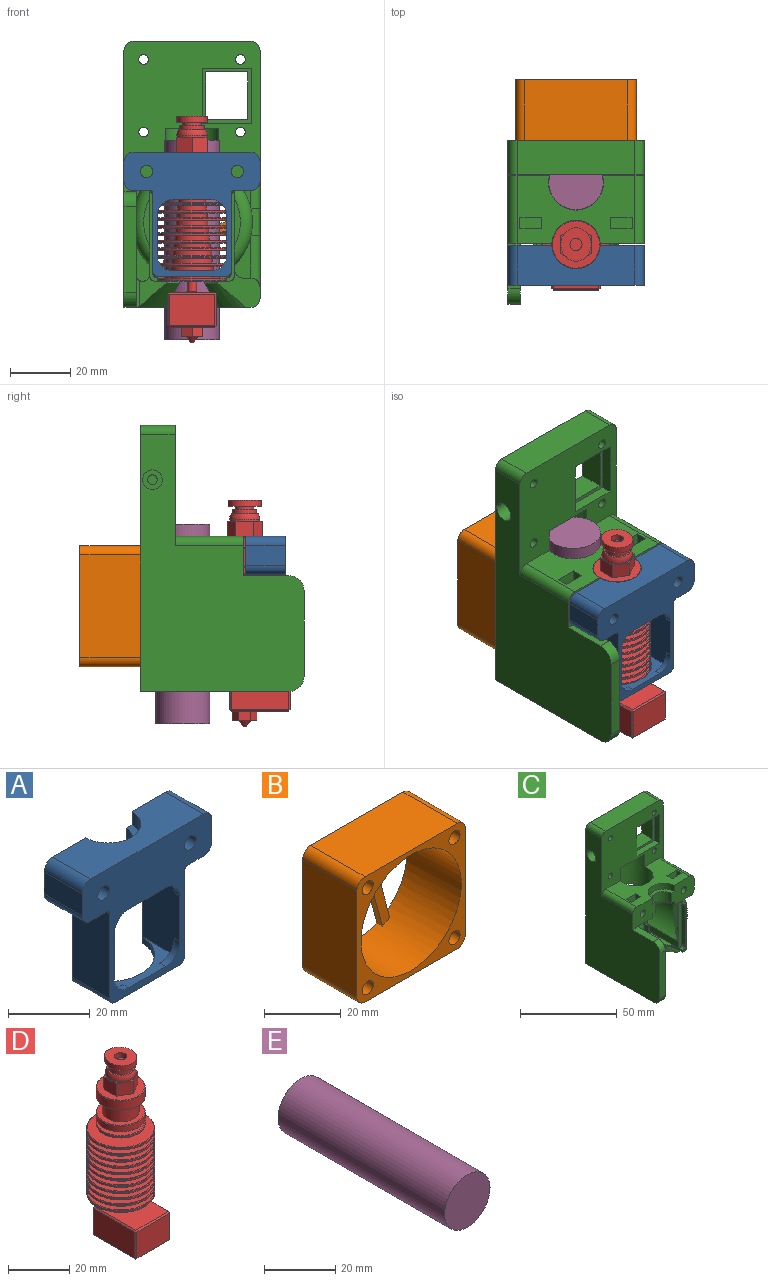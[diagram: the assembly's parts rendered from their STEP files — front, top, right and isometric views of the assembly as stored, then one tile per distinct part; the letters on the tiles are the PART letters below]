
ASSEMBLY  parts=5 mates=8
PART A: 39 faces, bbox 45x13.2x41.2 mm
  f0: plane 5x5mm, normal (0,1,0), area 5.4mm2, adj f15,f24,f26
  f1: plane 26.6x13mm, normal (1,0,0), area 319.8mm2, adj f2,f20,f21,f23,f24,f25,f27,f29
  f2: plane 39x13.2mm, normal (0,0,-1), area 305.9mm2, adj f1,f6,f11,f12,f15,f18,f20,f21
  f3: plane 39x13.2mm, normal (0,0,1), area 419.1mm2, adj f10,f11,f12,f21,f32,f33
  f4: plane 13.2x6.6mm, normal (1,0,0), area 87.1mm2, adj f11,f21,f31,f32
  f5: plane 13.2x6.6mm, normal (-1,0,0), area 87.1mm2, adj f12,f21,f33,f34
  f6: cylinder r=8mm len=15.99mm, axis (0,0,-1), area 63.8mm2, adj f2,f7,f11,f12
  f7: plane 15.99x7.7mm, normal (0,0,-1), area 42.8mm2, adj f6,f8,f11,f12
  f8: cylinder r=6mm len=11.99mm, axis (0,0,-1), area 109.5mm2, adj f7,f9,f11,f12
  f9: plane 15.99x7.7mm, normal (0,0,1), area 42.8mm2, adj f8,f10,f11,f12
  f10: cylinder r=8mm len=15.99mm, axis (0,0,-1), area 98.1mm2, adj f3,f9,f11,f12
  f11: plane 16.51x12.6mm, normal (0,1,0), area 177.7mm2, adj f2,f3,f4,f6,f7,f8,f9,f10
  f12: plane 16.51x12.6mm, normal (0,1,0), area 177.7mm2, adj f2,f3,f5,f6,f7,f8,f9,f10
  f13: cylinder r=2.05mm len=13.2mm, axis (0,-1,0), area 170mm2, adj f12,f21
  f14: cylinder r=2.05mm len=13.2mm, axis (0,-1,0), area 170mm2, adj f11,f21
  f15: plane 26.6x13mm, normal (-1,0,0), area 319.8mm2, adj f0,f2,f18,f21,f23,f24,f26,f28
  f16: plane 22x10.51mm, normal (0,0,-1), area 94.5mm2, adj f21,f30,f35,f36
  f17: plane 25.6x13mm, normal (1,0,0), area 332.8mm2, adj f18,f21,f36,f38
  f18: plane 28.56x2.61mm, normal (0,1,0), area 45.1mm2, adj f2,f15,f17,f24,f30,f36,f38
  f19: plane 25.6x13mm, normal (-1,0,0), area 332.8mm2, adj f20,f21,f35,f37
  f20: plane 28.56x2.61mm, normal (0,1,0), area 45.1mm2, adj f1,f2,f19,f24,f30,f35,f37
  f21: plane 45x41.2mm, normal (0,-1,0), area 758.6mm2, adj f1,f2,f3,f4,f5,f13,f14,f15
  f22: plane 12.8x2mm, normal (0,0,-1), area 25.6mm2, adj f21,f23,f28,f29
  f23: plane 22.8x8mm, normal (0,1,0), area 79.1mm2, adj f1,f2,f15,f22,f28,f29
  f24: plane 22.8x13mm, normal (0,0,1), area 83.7mm2, adj f0,f1,f15,f18,f20,f21,f25,f26
  f25: plane 5x5mm, normal (0,1,0), area 5.4mm2, adj f1,f24,f27
  f26: cylinder r=5mm len=5mm, axis (0,-1,0), area 15.7mm2, adj f0,f15,f21,f24
  f27: cylinder r=5mm len=5mm, axis (0,1,0), area 15.7mm2, adj f1,f21,f24,f25
  f28: cylinder r=5mm len=5mm, axis (0,1,0), area 15.7mm2, adj f15,f21,f22,f23
  f29: cylinder r=5mm len=5mm, axis (0,-1,0), area 15.7mm2, adj f1,f21,f22,f23
  f30: cylinder r=11.4mm len=22.78mm, axis (0,0,-1), area 69.5mm2, adj f16,f18,f20,f24,f35,f36
  f31: cylinder r=3mm len=13.2mm, axis (0,-1,0), area 62.2mm2, adj f2,f4,f11,f21
  f32: cylinder r=3mm len=13.2mm, axis (0,1,0), area 62.2mm2, adj f3,f4,f11,f21
  f33: cylinder r=3mm len=13.2mm, axis (0,-1,0), area 62.2mm2, adj f3,f5,f12,f21
  f34: cylinder r=3mm len=13.2mm, axis (0,1,0), area 62.2mm2, adj f2,f5,f12,f21
  f35: cylinder r=2mm len=13mm, axis (0,1,0), area 40.2mm2, adj f16,f19,f20,f21,f30
  f36: cylinder r=2mm len=13mm, axis (0,-1,0), area 40.2mm2, adj f16,f17,f18,f21,f30
  f37: cylinder r=1mm len=13mm, axis (0,-1,0), area 20.4mm2, adj f2,f19,f20,f21
  f38: cylinder r=1mm len=13mm, axis (0,1,0), area 20.4mm2, adj f2,f17,f18,f21
PART B: 25 faces, bbox 40x20x40 mm
  f0: plane 34x20mm, normal (0,0,-1), area 680mm2, adj f9,f10,f21,f24
  f1: plane 34x20mm, normal (1,0,0), area 680mm2, adj f9,f10,f21,f22
  f2: plane 34x20mm, normal (0,0,1), area 680mm2, adj f9,f10,f22,f23
  f3: cylinder r=18.5mm len=37mm, axis (0,1,0), area 2306.3mm2, adj f9,f10,f12,f13,f15,f16,f18,f19
  f4: cylinder r=2.05mm len=20mm, axis (0,1,0), area 257.6mm2, adj f9,f10
  f5: cylinder r=2.05mm len=20mm, axis (0,1,0), area 257.6mm2, adj f9,f10
  f6: cylinder r=2.05mm len=20mm, axis (0,1,0), area 257.6mm2, adj f9,f10
  f7: cylinder r=2.05mm len=20mm, axis (0,1,0), area 257.6mm2, adj f9,f10
  f8: plane 34x20mm, normal (-1,0,0), area 680mm2, adj f9,f10,f23,f24
  f9: plane 40x40mm, normal (0,-1,0), area 464.3mm2, adj f0,f1,f2,f3,f4,f5,f6,f7
  f10: plane 40x40mm, normal (0,1,0), area 702.9mm2, adj f0,f1,f2,f3,f4,f5,f6,f7
  f11: cylinder r=6mm len=5.91mm, axis (0,1,0), area 15.5mm2, adj f10,f12,f19,f20
  f12: plane 9.16x9.16mm, normal (0.71,0,-0.71), area 25.9mm2, adj f3,f10,f11,f20
  f13: plane 11.21x11.21mm, normal (-0.71,0,0.71), area 31.7mm2, adj f3,f10,f14,f20
  f14: cylinder r=6mm len=6.56mm, axis (0,1,0), area 15.5mm2, adj f10,f13,f15,f20
  f15: plane 12.52x3.35mm, normal (0.26,0,0.97), area 25.9mm2, adj f3,f10,f14,f20
  f16: plane 15.31x4.1mm, normal (-0.26,0,-0.97), area 31.7mm2, adj f3,f10,f17,f20
  f17: cylinder r=6mm len=7.2mm, axis (0,1,0), area 15.5mm2, adj f10,f16,f18,f20
  f18: plane 12.52x3.35mm, normal (-0.97,0,-0.26), area 25.9mm2, adj f3,f10,f17,f20
  f19: plane 15.31x4.1mm, normal (0.97,0,0.26), area 31.7mm2, adj f3,f10,f11,f20
  f20: plane 33.46x29.5mm, normal (0,-1,0), area 238.6mm2, adj f3,f11,f12,f13,f14,f15,f16,f17
  f21: cylinder r=3mm len=20mm, axis (0,-1,0), area 94.2mm2, adj f0,f1,f9,f10
  f22: cylinder r=3mm len=20mm, axis (0,1,0), area 94.2mm2, adj f1,f2,f9,f10
  f23: cylinder r=3mm len=20mm, axis (0,-1,0), area 94.2mm2, adj f2,f8,f9,f10
  f24: cylinder r=3mm len=20mm, axis (0,1,0), area 94.2mm2, adj f0,f8,f9,f10
PART C: 147 faces, bbox 46.5x58.5x89.5 mm
  f0: plane 11.9x4.4mm, normal (0,-1,0), area 34.1mm2, adj f2,f5,f19,f109,f141,f145
  f1: plane 10.46x9.18mm, normal (0,-1,0), area 42.6mm2, adj f5,f65,f88,f102,f107,f109,f144,f145
  f2: cylinder r=20mm len=22.2mm, axis (0,1,0), area 177mm2, adj f0,f4,f19,f141
  f3: cylinder r=20mm len=22.2mm, axis (0,1,0), area 72.4mm2, adj f4,f21,f22,f141
  f4: torus R=16mm, axis (0,-1,0), area 107.7mm2, adj f2,f3,f19,f21,f23,f28,f84,f106
  f5: plane 18.7x0.4mm, normal (0,0,1), area 7.5mm2, adj f0,f1,f109,f145
  f6: plane 88.6x45.6mm, normal (0,1,0), area 2644.8mm2, adj f11,f12,f13,f14,f16,f26,f46,f47
  f7: plane 28.3x4mm, normal (0,-1,0), area 113.2mm2, adj f46,f141,f142,f143
  f8: cylinder r=1.6mm len=7.6mm, axis (1,0,0), area 76.4mm2, adj f134,f137
  f9: cylinder r=1.6mm len=7mm, axis (1,0,0), area 70.4mm2, adj f13,f136
  f10: plane 45x39.7mm, normal (0,-1,0), area 1182.7mm2, adj f15,f16,f38,f46,f47,f98,f99,f123
  f11: plane 15.8x8mm, normal (-1,0,0), area 126.4mm2, adj f6,f12,f14,f133
  f12: plane 13.9x8mm, normal (0,0,1), area 111.2mm2, adj f6,f11,f13,f133
  f13: plane 15.8x8mm, normal (1,0,0), area 118.4mm2, adj f6,f9,f12,f14,f133
  f14: plane 13.9x8mm, normal (0,0,-1), area 111.2mm2, adj f6,f11,f13,f133
  f15: plane 39x22.7mm, normal (0,0,1), area 560.6mm2, adj f10,f27,f28,f38,f40,f50,f51,f52
  f16: plane 82x34.2mm, normal (1,0,0), area 864.4mm2, adj f6,f10,f27,f92,f93,f94,f95,f96
  f17: cylinder r=1.6mm len=4.4mm, axis (1,0,0), area 44.2mm2, adj f120,f121
  f18: plane 5x2.15mm, normal (-1,0,0), area 10.7mm2, adj f112,f113,f114,f118
  f19: plane 29.2x27.6mm, normal (-1,0,0), area 175mm2, adj f0,f2,f4,f23,f85,f102,f106,f109
  f20: plane 26.2x0.4mm, normal (1,0,0), area 10.5mm2, adj f21,f22,f28,f90
  f21: plane 26.2x8.43mm, normal (0,0,-1), area 95.2mm2, adj f3,f4,f20,f22,f28
  f22: plane 3.48x2.9mm, normal (0,-1,0), area 2.8mm2, adj f3,f20,f21,f90,f141
  f23: plane 15.13x1.9mm, normal (0,-1,0), area 19.4mm2, adj f4,f19
  f24: plane 15.13x1.9mm, normal (0,-1,0), area 19.4mm2, adj f76,f100
  f25: plane 6.06x2.48mm, normal (0,-1,0), area 6.3mm2, adj f32,f75,f93
  f26: plane 49.15x42mm, normal (0,0,-1), area 738mm2, adj f6,f46,f63,f68,f97,f107,f108,f115
  f27: plane 41.59x16.51mm, normal (0,-1,0), area 228.3mm2, adj f15,f16,f31,f32,f39,f40,f41,f42
  f28: plane 41.59x16.51mm, normal (0,-1,0), area 231mm2, adj f4,f15,f20,f21,f31,f40,f41,f42
  f29: plane 3.8x0.1mm, normal (0,1,0), area 0.2mm2, adj f69,f80
  f30: plane 18.7x2.4mm, normal (0,0,1), area 44.9mm2, adj f36,f68,f91,f96
  f31: plane 26.2x23.77mm, normal (0,0,-1), area 294.8mm2, adj f27,f28,f38,f44,f70,f73,f74,f77
  f32: plane 26.2x7.43mm, normal (0,0,-1), area 69mm2, adj f25,f27,f75,f92,f100
  f33: plane 24.37x7.02mm, normal (0,0,1), area 75mm2, adj f34,f63,f64,f65,f104
  f34: plane 4.56x3.93mm, normal (0,-1,0), area 11.3mm2, adj f33,f63,f69,f78,f104
  f35: plane 4.56x3.93mm, normal (0,-1,0), area 11.3mm2, adj f37,f63,f69,f73,f103
  f36: plane 14.06x5.4mm, normal (0,-1,0), area 41.8mm2, adj f30,f75,f76,f91,f95
  f37: plane 24.37x7.02mm, normal (0,0,1), area 75mm2, adj f35,f63,f66,f67,f103
  f38: cylinder r=9.1mm len=20.6mm, axis (0,0,1), area 886.5mm2, adj f10,f15,f31,f70,f146
  f39: cylinder r=2.05mm len=5mm, axis (0,-1,0), area 64.4mm2, adj f27,f54
  f40: cylinder r=8mm len=15.99mm, axis (0,0,-1), area 98.1mm2, adj f15,f27,f28,f41
  f41: plane 15.99x7.7mm, normal (0,0,1), area 42.8mm2, adj f27,f28,f40,f42
  f42: cylinder r=6mm len=11.99mm, axis (0,0,-1), area 109.5mm2, adj f27,f28,f41,f43
  f43: plane 15.99x7.7mm, normal (0,0,-1), area 42.8mm2, adj f27,f28,f42,f44
  f44: cylinder r=8mm len=15.99mm, axis (0,0,-1), area 63.8mm2, adj f27,f28,f31,f43
  f45: plane 10.34x3.7mm, normal (1,0,0), area 36.7mm2, adj f68,f96,f97,f122
  f46: plane 85x54.15mm, normal (-1,0,0), area 2794.1mm2, adj f6,f7,f10,f26,f28,f90,f99,f123
  f47: plane 39x11.5mm, normal (0,0,1), area 448.5mm2, adj f6,f10,f98,f99
  f48: cylinder r=2.05mm len=5mm, axis (0,-1,0), area 64.4mm2, adj f28,f51
  f49: plane 7.1x3.8mm, normal (0,0,1), area 27mm2, adj f50,f51,f52,f53
  f50: plane 10.8x3.8mm, normal (-1,0,0), area 41mm2, adj f15,f49,f51,f53
  f51: plane 10.8x7.1mm, normal (0,1,0), area 63.5mm2, adj f15,f48,f49,f50,f52
  f52: plane 10.8x3.8mm, normal (1,0,0), area 41mm2, adj f15,f49,f51,f53
  f53: plane 10.8x7.1mm, normal (0,-1,0), area 63.5mm2, adj f15,f49,f50,f52,f60
  f54: plane 10.8x7.1mm, normal (0,1,0), area 63.5mm2, adj f15,f39,f56,f57,f58
  f55: plane 10.8x7.1mm, normal (0,-1,0), area 63.5mm2, adj f15,f56,f57,f58,f62
  f56: plane 7.1x3.8mm, normal (0,0,1), area 27mm2, adj f54,f55,f57,f58
  f57: plane 10.8x3.8mm, normal (1,0,0), area 41mm2, adj f15,f54,f55,f56
  f58: plane 10.8x3.8mm, normal (-1,0,0), area 41mm2, adj f15,f54,f55,f56
  f59: plane 4.1x4.1mm, normal (0,-1,0), area 13.2mm2, adj f60
  f60: cylinder r=2.05mm len=4.1mm, axis (0,-1,0), area 30.9mm2, adj f53,f59
  f61: plane 4.1x4.1mm, normal (0,-1,0), area 13.2mm2, adj f62
  f62: cylinder r=2.05mm len=4.1mm, axis (0,-1,0), area 30.9mm2, adj f55,f61
  f63: cylinder r=9.1mm len=18.2mm, axis (0,0,1), area 333.8mm2, adj f26,f33,f34,f35,f37,f64,f66,f69
  f64: plane 7.52x4.9mm, normal (0.82,0.57,0), area 25.6mm2, adj f33,f63,f65,f107
  f65: cylinder r=11.4mm len=10.61mm, axis (0,0,-1), area 17.2mm2, adj f1,f33,f64,f88,f89,f104,f107
  f66: plane 7.52x4.9mm, normal (-0.82,0.57,0), area 25.6mm2, adj f37,f63,f67,f108
  f67: cylinder r=11.4mm len=10.61mm, axis (0,0,-1), area 17.2mm2, adj f37,f66,f68,f86,f87,f103,f108
  f68: plane 15.69x14.21mm, normal (0,-1,0), area 91.6mm2, adj f26,f30,f45,f67,f76,f86,f91,f96
  f69: cylinder r=18.5mm len=37mm, axis (0,-1,0), area 1412.8mm2, adj f6,f29,f34,f35,f63,f71,f72,f73
  f70: plane 23.77x8mm, normal (0,0.57,-0.82), area 151.8mm2, adj f6,f31,f38,f71,f72
  f71: bspline ~13.74x11.32mm, area 62.1mm2, adj f6,f69,f70,f74
  f72: bspline ~13.74x11.32mm, area 62.1mm2, adj f6,f69,f70,f77
  f73: plane 28.99x26.2mm, normal (-1,0,0), area 132.8mm2, adj f27,f31,f35,f69,f81,f103
  f74: extruded ~24.31x5.61mm, area 150.1mm2, adj f31,f69,f71,f81
  f75: cylinder r=20mm len=24.68mm, axis (0,1,0), area 595.4mm2, adj f25,f32,f36,f76,f94,f100
  f76: plane 29.2x27.6mm, normal (1,0,0), area 137.6mm2, adj f24,f36,f68,f75,f83,f91,f100,f101
  f77: extruded ~24.31x5.61mm, area 155.1mm2, adj f31,f69,f72,f80
  f78: plane 28.99x26.2mm, normal (1,0,0), area 132.8mm2, adj f28,f31,f34,f69,f80,f104
  f79: plane 3.8x0.1mm, normal (0,1,0), area 0.2mm2, adj f69,f81
  f80: plane 26.43x11.36mm, normal (0.82,0.57,0), area 231.6mm2, adj f29,f31,f69,f77,f78
  f81: plane 25.41x10.34mm, normal (-0.82,0.57,0), area 231.6mm2, adj f31,f69,f73,f74,f79
  f82: plane 25.61x3mm, normal (-1,0,0), area 76.8mm2, adj f27,f83,f100,f103,f105
  f83: plane 29.6x2.7mm, normal (0,-1,0), area 28.2mm2, adj f76,f82,f86,f87,f101,f103,f105
  f84: plane 25.61x3mm, normal (1,0,0), area 76.8mm2, adj f4,f28,f85,f104,f106
  f85: plane 29.6x2.7mm, normal (0,-1,0), area 28.2mm2, adj f19,f84,f88,f89,f102,f104,f106
  f86: plane 10.5x3.78mm, normal (0,0,-1), area 14.9mm2, adj f67,f68,f83,f87,f101
  f87: plane 2.7x1.01mm, normal (-1,0,0), area 2.7mm2, adj f67,f83,f86,f103
  f88: plane 10.5x3.78mm, normal (0,0,-1), area 14.9mm2, adj f1,f65,f85,f89,f102
  f89: plane 2.7x1.01mm, normal (1,0,0), area 2.7mm2, adj f65,f85,f88,f104
  f90: plane 41.15x4mm, normal (0,0,1), area 112.2mm2, adj f20,f22,f28,f46,f141,f143
  f91: cylinder r=3mm len=18.7mm, axis (0,1,0), area 88.1mm2, adj f30,f36,f68,f76
  f92: cylinder r=3mm len=29.2mm, axis (0,1,0), area 130.5mm2, adj f16,f27,f32,f93
  f93: cylinder r=3mm len=9.06mm, axis (0,0,-1), area 35.6mm2, adj f16,f25,f92,f94
  f94: bspline ~11.65x3.39mm, area 38.9mm2, adj f16,f75,f93,f95
  f95: cylinder r=3mm len=17.06mm, axis (0,0,-1), area 73.3mm2, adj f16,f36,f94,f96
  f96: cylinder r=3mm len=21.7mm, axis (0,-1,0), area 92.4mm2, adj f16,f30,f45,f68,f95,f122
  f97: cylinder r=3mm len=26.7mm, axis (0,-1,0), area 122mm2, adj f6,f16,f26,f45,f68,f122
  f98: cylinder r=3mm len=11.5mm, axis (0,1,0), area 54.2mm2, adj f6,f10,f16,f47
  f99: cylinder r=3mm len=11.5mm, axis (0,-1,0), area 54.2mm2, adj f6,f10,f46,f47
  f100: torus R=16mm, axis (0,-1,0), area 150.7mm2, adj f24,f27,f32,f75,f76,f82,f105
  f101: cylinder r=2mm len=10.5mm, axis (0,1,0), area 33mm2, adj f68,f76,f83,f86
  f102: cylinder r=2mm len=10.5mm, axis (0,1,0), area 33mm2, adj f1,f19,f85,f88
  f103: cylinder r=2mm len=29.2mm, axis (0,1,0), area 13.9mm2, adj f27,f35,f37,f67,f73,f82,f83,f87
  f104: cylinder r=2mm len=29.2mm, axis (0,-1,0), area 13.9mm2, adj f28,f33,f34,f65,f78,f84,f85,f89
  f105: cylinder r=1mm len=3.23mm, axis (0,-1,0), area 4.6mm2, adj f76,f82,f83,f100
  f106: cylinder r=1mm len=3.23mm, axis (0,-1,0), area 4.6mm2, adj f4,f19,f84,f85
  f107: cone r=11.4mm half-angle=45deg, axis (0,0,-1), area 105.5mm2, adj f1,f26,f63,f64,f65,f144
  f108: cone r=11.4mm half-angle=45deg, axis (0,0,-1), area 99.4mm2, adj f26,f63,f66,f67,f68
  f109: cylinder r=2mm len=18.7mm, axis (0,-1,0), area 58.8mm2, adj f0,f1,f5,f19
  f110: plane 5x4mm, normal (0,1,0), area 20mm2, adj f63,f111,f113,f114
  f111: plane 5x2.15mm, normal (-1,0,0), area 10.7mm2, adj f110,f113,f114,f119
  f112: plane 5x4mm, normal (0,-1,0), area 20mm2, adj f18,f63,f113,f114
  f113: plane 10x4mm, normal (0,0,-1), area 29.8mm2, adj f18,f63,f110,f111,f112,f117
  f114: plane 10x4mm, normal (0,0,1), area 29.8mm2, adj f18,f63,f110,f111,f112,f115
  f115: plane 5.7x2.35mm, normal (1,0,0), area 13.4mm2, adj f26,f114,f118,f119
  f116: plane 5.7x2.5mm, normal (0,0,-1), area 14.3mm2, adj f117,f118,f119,f120
  f117: plane 5.7x2.35mm, normal (1,0,0), area 13.4mm2, adj f113,f116,f118,f119
  f118: plane 9.7x2.5mm, normal (0,-1,0), area 24.3mm2, adj f18,f26,f115,f116,f117,f120
  f119: plane 9.7x2.5mm, normal (0,1,0), area 24.3mm2, adj f26,f111,f115,f116,f117,f120
  f120: plane 9.7x5.7mm, normal (-1,0,0), area 47.2mm2, adj f17,f26,f116,f118,f119
  f121: plane 6x6mm, normal (1,0,0), area 20.2mm2, adj f17,f122
  f122: cylinder r=3mm len=6mm, axis (1,0,0), area 74.8mm2, adj f16,f45,f96,f97,f121
  f123: cylinder r=3mm len=22.7mm, axis (0,1,0), area 107mm2, adj f10,f15,f28,f46
  f124: cylinder r=3mm len=22.7mm, axis (0,-1,0), area 107mm2, adj f10,f15,f16,f27
  f125: cylinder r=1.6mm len=11.5mm, axis (0,1,0), area 115.6mm2, adj f6,f10
  f126: cylinder r=1.6mm len=11.5mm, axis (0,1,0), area 115.6mm2, adj f6,f10
  f127: cylinder r=1.6mm len=11.5mm, axis (0,1,0), area 115.6mm2, adj f6,f10
  f128: cylinder r=1.6mm len=11.5mm, axis (0,1,0), area 115.6mm2, adj f6,f10
  f129: plane 18.2x3.5mm, normal (-1,0,0), area 63.7mm2, adj f10,f130,f132,f133
  f130: plane 16.3x3.5mm, normal (0,0,1), area 57mm2, adj f10,f129,f131,f133
  f131: plane 18.2x3.5mm, normal (1,0,0), area 63.7mm2, adj f10,f130,f132,f133
  f132: plane 16.3x3.5mm, normal (0,0,-1), area 57mm2, adj f10,f129,f131,f133
  f133: plane 18.2x16.3mm, normal (0,-1,0), area 77mm2, adj f11,f12,f13,f14,f129,f130,f131,f132
  f134: plane 6.5x6.5mm, normal (-1,0,0), area 25.1mm2, adj f8,f135
  f135: cylinder r=3.25mm len=10mm, axis (-1,0,0), area 204.2mm2, adj f46,f134
  f136: plane 7.5x5.6mm, normal (-1,0,0), area 34mm2, adj f6,f9,f138,f139,f140
  f137: plane 7.5x5.6mm, normal (1,0,0), area 34mm2, adj f6,f8,f138,f139,f140
  f138: plane 7.5x2.5mm, normal (0,0,1), area 18.8mm2, adj f6,f136,f137,f140
  f139: plane 7.5x2.5mm, normal (0,0,-1), area 18.8mm2, adj f6,f136,f137,f140
  f140: plane 5.6x2.5mm, normal (0,1,0), area 14mm2, adj f136,f137,f138,f139
  f141: plane 46.15x38.3mm, normal (1,0,0), area 1170.4mm2, adj f0,f2,f3,f4,f7,f22,f26,f90
  f142: cylinder r=5mm len=5mm, axis (-1,0,0), area 31.4mm2, adj f7,f26,f46,f141
  f143: cylinder r=5mm len=5mm, axis (-1,0,0), area 31.4mm2, adj f7,f46,f90,f141
  f144: cylinder r=1mm len=10.7mm, axis (0,0,1), area 15.4mm2, adj f1,f26,f107,f141,f145
  f145: cylinder r=2mm len=19.7mm, axis (0,1,0), area 59.8mm2, adj f0,f1,f5,f141,f144
  f146: plane 17.5x6.6mm, normal (0,0,-1), area 85.2mm2, adj f10,f38
PART D: 145 faces, bbox 22.3x26.2x74.9 mm
  f0: plane 4.33x2.5mm, normal (0,0,1), area 1.3mm2, adj f130,f131,f134
  f1: plane 5x1.44mm, normal (0,0,1), area 1.3mm2, adj f129,f130,f134
  f2: plane 4.33x2.5mm, normal (0,0,1), area 1.3mm2, adj f128,f129,f134
  f3: plane 4.33x2.5mm, normal (0,0,1), area 1.3mm2, adj f127,f128,f134
  f4: plane 5x1.44mm, normal (0,0,1), area 1.3mm2, adj f127,f132,f134
  f5: plane 19x15mm, normal (0,0,-1), area 242.6mm2, adj f103,f108,f111,f114,f116,f117,f118,f119
  f6: plane 15.6x15.6mm, normal (0,0,1), area 104.5mm2, adj f89,f127,f128,f129,f130,f131,f132
  f7: cylinder r=1.5mm len=3.3mm, axis (0,0,-1), area 31.1mm2, adj f8,f115
  f8: plane 21.9x21.9mm, normal (0,0,-1), area 369.6mm2, adj f7,f62
  f9: cylinder r=11.15mm len=22.3mm, axis (0,0,-1), area 42mm2, adj f62,f63
  f10: plane 21.9x21.9mm, normal (0,0,1), area 200mm2, adj f11,f63
  f11: cylinder r=7.5mm len=15mm, axis (0,0,-1), area 70.7mm2, adj f10,f12
  f12: plane 21.9x21.9mm, normal (0,0,-1), area 200mm2, adj f11,f64
  f13: cylinder r=11.15mm len=22.3mm, axis (0,0,-1), area 42mm2, adj f64,f65
  f14: plane 21.9x21.9mm, normal (0,0,1), area 222.7mm2, adj f15,f65
  f15: cylinder r=7mm len=14mm, axis (0,0,-1), area 66mm2, adj f14,f16
  f16: plane 21.9x21.9mm, normal (0,0,-1), area 222.7mm2, adj f15,f66
  f17: cylinder r=11.15mm len=22.3mm, axis (0,0,-1), area 42mm2, adj f66,f67
  f18: plane 21.9x21.9mm, normal (0,0,1), area 233.5mm2, adj f19,f67
  f19: cylinder r=6.75mm len=13.5mm, axis (0,0,-1), area 63.6mm2, adj f18,f20
  f20: plane 21.9x21.9mm, normal (0,0,-1), area 233.5mm2, adj f19,f68
  f21: cylinder r=11.15mm len=22.3mm, axis (0,0,-1), area 42mm2, adj f68,f69
  f22: plane 21.9x21.9mm, normal (0,0,1), area 244mm2, adj f23,f69
  f23: cylinder r=6.5mm len=13mm, axis (0,0,-1), area 61.3mm2, adj f22,f24
  f24: plane 21.9x21.9mm, normal (0,0,-1), area 244mm2, adj f23,f70
  f25: cylinder r=11.15mm len=22.3mm, axis (0,0,-1), area 42mm2, adj f70,f71
  f26: plane 21.9x21.9mm, normal (0,0,1), area 263.6mm2, adj f27,f71
  f27: cylinder r=6mm len=12mm, axis (0,0,-1), area 56.5mm2, adj f26,f28
  f28: plane 21.9x21.9mm, normal (0,0,-1), area 263.6mm2, adj f27,f72
  f29: cylinder r=11.15mm len=22.3mm, axis (0,0,-1), area 42mm2, adj f72,f73
  f30: plane 21.9x21.9mm, normal (0,0,1), area 272.8mm2, adj f31,f73
  f31: cylinder r=5.75mm len=11.5mm, axis (0,0,-1), area 54.2mm2, adj f30,f32
  f32: plane 21.9x21.9mm, normal (0,0,-1), area 272.8mm2, adj f31,f74
  f33: cylinder r=11.15mm len=22.3mm, axis (0,0,-1), area 42mm2, adj f74,f75
  f34: plane 21.9x21.9mm, normal (0,0,1), area 281.7mm2, adj f35,f75
  f35: cylinder r=5.5mm len=11mm, axis (0,0,-1), area 51.8mm2, adj f34,f36
  f36: plane 21.9x21.9mm, normal (0,0,-1), area 281.7mm2, adj f35,f76
  f37: cylinder r=11.15mm len=22.3mm, axis (0,0,-1), area 42mm2, adj f76,f77
  f38: plane 21.9x21.9mm, normal (0,0,1), area 290.1mm2, adj f39,f77
  f39: cylinder r=5.25mm len=10.5mm, axis (0,0,-1), area 49.5mm2, adj f38,f40
  f40: plane 21.9x21.9mm, normal (0,0,-1), area 290.1mm2, adj f39,f78
  f41: cylinder r=11.15mm len=22.3mm, axis (0,0,-1), area 42mm2, adj f78,f79
  f42: plane 21.9x21.9mm, normal (0,0,1), area 298.1mm2, adj f43,f79
  f43: cylinder r=5mm len=10mm, axis (0,0,-1), area 47.1mm2, adj f42,f44
  f44: plane 21.9x21.9mm, normal (0,0,-1), area 298.1mm2, adj f43,f80
  f45: cylinder r=11.15mm len=22.3mm, axis (0,0,-1), area 42mm2, adj f80,f81
  f46: plane 21.9x21.9mm, normal (0,0,1), area 305.8mm2, adj f47,f81
  f47: cylinder r=4.75mm len=9.5mm, axis (0,0,-1), area 44.8mm2, adj f46,f48
  f48: plane 21.9x21.9mm, normal (0,0,-1), area 305.8mm2, adj f47,f82
  f49: cylinder r=11.15mm len=22.3mm, axis (0,0,-1), area 42mm2, adj f82,f83
  f50: plane 21.9x21.9mm, normal (0,0,1), area 313.1mm2, adj f51,f83
  f51: cylinder r=4.5mm len=9mm, axis (0,0,-1), area 42.4mm2, adj f50,f52
  f52: plane 15.6x15.6mm, normal (0,0,-1), area 127.5mm2, adj f51,f84
  f53: cylinder r=8mm len=16mm, axis (0,0,-1), area 30.2mm2, adj f84,f85
  f54: plane 15.6x15.6mm, normal (0,0,1), area 127.5mm2, adj f55,f85
  f55: cylinder r=4.5mm len=9mm, axis (0,0,-1), area 42.4mm2, adj f54,f56
  f56: plane 15.6x15.6mm, normal (0,0,-1), area 127.5mm2, adj f55,f86
  f57: cylinder r=8mm len=16mm, axis (0,0,-1), area 110.6mm2, adj f86,f87
  f58: plane 15.6x15.6mm, normal (0,0,1), area 78mm2, adj f59,f87
  f59: cylinder r=6mm len=12mm, axis (0,0,-1), area 226.2mm2, adj f58,f60
  f60: plane 15.6x15.6mm, normal (0,0,-1), area 78mm2, adj f59,f88
  f61: cylinder r=8mm len=16mm, axis (0,0,-1), area 181mm2, adj f88,f89
  f62: cone r=10.95mm half-angle=45deg, axis (0,0,1), area 19.6mm2, adj f8,f9
  f63: cone r=11.15mm half-angle=45deg, axis (0,0,-1), area 19.6mm2, adj f9,f10
  f64: cone r=10.95mm half-angle=45deg, axis (0,0,1), area 19.6mm2, adj f12,f13
  f65: cone r=11.15mm half-angle=45deg, axis (0,0,-1), area 19.6mm2, adj f13,f14
  f66: cone r=10.95mm half-angle=45deg, axis (0,0,1), area 19.6mm2, adj f16,f17
  f67: cone r=11.15mm half-angle=45deg, axis (0,0,-1), area 19.6mm2, adj f17,f18
  f68: cone r=10.95mm half-angle=45deg, axis (0,0,1), area 19.6mm2, adj f20,f21
  f69: cone r=11.15mm half-angle=45deg, axis (0,0,-1), area 19.6mm2, adj f21,f22
  f70: cone r=10.95mm half-angle=45deg, axis (0,0,1), area 19.6mm2, adj f24,f25
  f71: cone r=11.15mm half-angle=45deg, axis (0,0,-1), area 19.6mm2, adj f25,f26
  f72: cone r=10.95mm half-angle=45deg, axis (0,0,1), area 19.6mm2, adj f28,f29
  f73: cone r=11.15mm half-angle=45deg, axis (0,0,-1), area 19.6mm2, adj f29,f30
  f74: cone r=10.95mm half-angle=45deg, axis (0,0,1), area 19.6mm2, adj f32,f33
  f75: cone r=11.15mm half-angle=45deg, axis (0,0,-1), area 19.6mm2, adj f33,f34
  f76: cone r=10.95mm half-angle=45deg, axis (0,0,1), area 19.6mm2, adj f36,f37
  f77: cone r=11.15mm half-angle=45deg, axis (0,0,-1), area 19.6mm2, adj f37,f38
  f78: cone r=10.95mm half-angle=45deg, axis (0,0,1), area 19.6mm2, adj f40,f41
  f79: cone r=11.15mm half-angle=45deg, axis (0,0,-1), area 19.6mm2, adj f41,f42
  f80: cone r=10.95mm half-angle=45deg, axis (0,0,1), area 19.6mm2, adj f44,f45
  f81: cone r=11.15mm half-angle=45deg, axis (0,0,-1), area 19.6mm2, adj f45,f46
  f82: cone r=10.95mm half-angle=45deg, axis (0,0,1), area 19.6mm2, adj f48,f49
  f83: cone r=11.15mm half-angle=45deg, axis (0,0,-1), area 19.6mm2, adj f49,f50
  f84: cone r=7.8mm half-angle=45deg, axis (0,0,1), area 14mm2, adj f52,f53
  f85: cone r=8mm half-angle=45deg, axis (0,0,-1), area 14mm2, adj f53,f54
  f86: cone r=7.8mm half-angle=45deg, axis (0,0,1), area 14mm2, adj f56,f57
  f87: cone r=8mm half-angle=45deg, axis (0,0,-1), area 14mm2, adj f57,f58
  f88: cone r=7.8mm half-angle=45deg, axis (0,0,1), area 14mm2, adj f60,f61
  f89: cone r=8mm half-angle=45deg, axis (0,0,-1), area 14mm2, adj f6,f61
  f90: plane 15x10.5mm, normal (0,1,0), area 157.5mm2, adj f98,f99,f108,f109
  f91: plane 19x10.5mm, normal (1,0,0), area 199.5mm2, adj f95,f98,f102,f103
  f92: plane 15x10.5mm, normal (0,-1,0), area 157.5mm2, adj f101,f102,f110,f111
  f93: plane 19x10.5mm, normal (-1,0,0), area 199.5mm2, adj f100,f109,f110,f114
  f94: plane 19x15mm, normal (0,0,1), area 272.4mm2, adj f95,f99,f100,f101,f115
  f95: plane 19x0.5mm, normal (0.71,0,0.71), area 13.4mm2, adj f91,f94,f96,f97
  f96: plane 0.5x0.5mm, normal (0.58,0.58,0.58), area 0.2mm2, adj f95,f98,f99
  f97: plane 0.5x0.5mm, normal (0.58,-0.58,0.58), area 0.2mm2, adj f95,f101,f102
  f98: plane 10.5x0.5mm, normal (0.71,0.71,0), area 7.4mm2, adj f90,f91,f96,f104
  f99: plane 15x0.5mm, normal (0,0.71,0.71), area 10.6mm2, adj f90,f94,f96,f105
  f100: plane 19x0.5mm, normal (-0.71,0,0.71), area 13.4mm2, adj f93,f94,f105,f106
  f101: plane 15x0.5mm, normal (0,-0.71,0.71), area 10.6mm2, adj f92,f94,f97,f106
  f102: plane 10.5x0.5mm, normal (0.71,-0.71,0), area 7.4mm2, adj f91,f92,f97,f107
  f103: plane 19x0.5mm, normal (0.71,0,-0.71), area 13.4mm2, adj f5,f91,f104,f107
  f104: plane 0.5x0.5mm, normal (0.58,0.58,-0.58), area 0.2mm2, adj f98,f103,f108
  f105: plane 0.5x0.5mm, normal (-0.58,0.58,0.58), area 0.2mm2, adj f99,f100,f109
  f106: plane 0.5x0.5mm, normal (-0.58,-0.58,0.58), area 0.2mm2, adj f100,f101,f110
  f107: plane 0.5x0.5mm, normal (0.58,-0.58,-0.58), area 0.2mm2, adj f102,f103,f111
  f108: plane 15x0.5mm, normal (0,0.71,-0.71), area 10.6mm2, adj f5,f90,f104,f112
  f109: plane 10.5x0.5mm, normal (-0.71,0.71,0), area 7.4mm2, adj f90,f93,f105,f112
  f110: plane 10.5x0.5mm, normal (-0.71,-0.71,0), area 7.4mm2, adj f92,f93,f106,f113
  f111: plane 15x0.5mm, normal (0,-0.71,-0.71), area 10.6mm2, adj f5,f92,f107,f113
  f112: plane 0.5x0.5mm, normal (-0.58,0.58,-0.58), area 0.2mm2, adj f108,f109,f114
  f113: plane 0.5x0.5mm, normal (-0.58,-0.58,-0.58), area 0.2mm2, adj f110,f111,f114
  f114: plane 19x0.5mm, normal (-0.71,0,-0.71), area 13.4mm2, adj f5,f93,f112,f113
  f115: cone r=2mm half-angle=45deg, axis (0,0,-1), area 7.8mm2, adj f7,f94
  f116: plane 3.5x3mm, normal (0.5,0.87,0), area 12.1mm2, adj f5,f117,f121,f122
  f117: plane 4.04x3mm, normal (1,0,0), area 12.1mm2, adj f5,f116,f118,f122
  f118: plane 3.5x3mm, normal (0.5,-0.87,0), area 12.1mm2, adj f5,f117,f119,f122
  f119: plane 3.5x3mm, normal (-0.5,-0.87,0), area 12.1mm2, adj f5,f118,f120,f122
  f120: plane 4.04x3mm, normal (-1,0,0), area 12.1mm2, adj f5,f119,f121,f122
  f121: plane 3.5x3mm, normal (-0.5,0.87,0), area 12.1mm2, adj f5,f116,f120,f122
  f122: plane 8.08x7mm, normal (0,0,-1), area 26.5mm2, adj f116,f117,f118,f119,f120,f121,f123
  f123: cone r=0.5mm half-angle=41.2deg, axis (0,0,1), area 23mm2, adj f122,f124
  f124: plane 1x1mm, normal (0,0,-1), area 0.7mm2, adj f123,f125
  f125: cylinder r=0.2mm len=1.8mm, axis (0,0,1), area 2.3mm2, adj f124,f126
  f126: plane 0.4x0.4mm, normal (0,0,-1), area 0.1mm2, adj f125
  f127: plane 5x5mm, normal (0.5,-0.87,0), area 28.9mm2, adj f3,f4,f6,f128,f132
  f128: plane 5.77x5mm, normal (1,0,0), area 28.9mm2, adj f2,f3,f6,f127,f129
  f129: plane 5x5mm, normal (0.5,0.87,0), area 28.9mm2, adj f1,f2,f6,f128,f130
  f130: plane 5x5mm, normal (-0.5,0.87,0), area 28.9mm2, adj f0,f1,f6,f129,f131
  f131: plane 5.77x5mm, normal (-1,0,0), area 28.9mm2, adj f0,f6,f130,f132,f133
  f132: plane 5x5mm, normal (-0.5,-0.87,0), area 28.9mm2, adj f4,f6,f127,f131,f133
  f133: plane 4.33x2.5mm, normal (0,0,1), area 1.3mm2, adj f131,f132,f134
  f134: cylinder r=5mm len=10mm, axis (0,0,-1), area 15.7mm2, adj f0,f1,f2,f3,f4,f133,f135
  f135: torus R=0.75mm, axis (0,0,-1), area 63.2mm2, adj f134,f136
  f136: plane 9x9mm, normal (0,0,1), area 13.4mm2, adj f135,f137
  f137: cylinder r=4mm len=8mm, axis (0,0,-1), area 37.7mm2, adj f136,f138
  f138: plane 8x8mm, normal (0,0,1), area 22mm2, adj f137,f139
  f139: cylinder r=3mm len=6mm, axis (0,0,-1), area 18.8mm2, adj f138,f143
  f140: extruded ~11x10mm, area 66mm2, adj f142,f143
  f141: cylinder r=2mm len=4mm, axis (0,0,-1), area 25.1mm2, adj f142,f144
  f142: plane 11x10mm, normal (0,0,1), area 73.8mm2, adj f140,f141
  f143: plane 11x10mm, normal (0,0,-1), area 58.1mm2, adj f139,f140
  f144: plane 4x4mm, normal (0,0,1), area 12.6mm2, adj f141
PART E: 3 faces, bbox 18x66x18 mm
  f0: cylinder r=9mm len=66mm, axis (0,1,0), area 3732.2mm2, adj f1,f2
  f1: plane 18x18mm, normal (0,-1,0), area 254.5mm2, adj f0
  f2: plane 18x18mm, normal (0,1,0), area 254.5mm2, adj f0
PLACE A rot(axis=(0,0,1),0deg) t=(-6.27,-7.94,12.47)mm
PLACE B rot(axis=(0,0,-1),180deg) t=(-6.27,26.56,-4.33)mm
PLACE C rot(axis=(0,0,1),0deg) t=(-86.27,-7.94,12.47)mm fixed
PLACE D rot(axis=(0,0,1),0deg) t=(-6.27,-7.94,-27.63)mm
PLACE E rot(axis=(-1,0,0),90deg) t=(-6.27,12.56,-43.13)mm
MATE parallel A.f21 <-> C.f27  axis (0,-1,0) through (-6.27,-21.44,6.72)mm
MATE revolute C.f2 <-> B.f3  axis (0,1,0) through (-6.27,26.56,-4.33)mm
MATE slider E.f0 <-> C.f38  axis (0,0,1) through (-6.27,12.56,22.87)mm
MATE planar E.f0 <-> D.f7  axis (0,0,-1) through (-6.27,12.56,-43.13)mm
MATE parallel D.f92 <-> C.f10  axis (0,-1,0) through (-6.27,-22.94,-33.38)mm
MATE parallel B.f8 <-> C.f16  axis (1,0,0) through (13.73,36.56,-4.33)mm
MATE revolute A.f6 <-> D.f7  axis (0,0,1) through (-6.27,-7.94,14.77)mm
MATE revolute D.f7 <-> C.f40  axis (0,0,-1) through (-6.27,-7.94,14.77)mm
